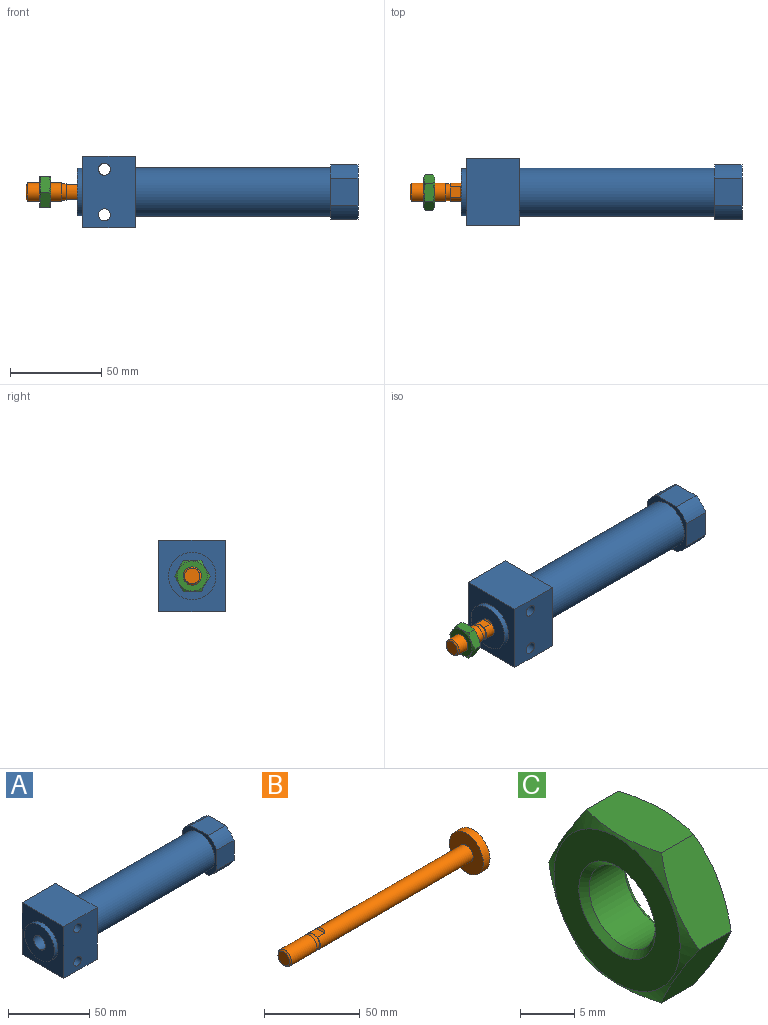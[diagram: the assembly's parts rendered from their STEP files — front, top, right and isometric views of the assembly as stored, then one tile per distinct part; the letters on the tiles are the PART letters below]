
ASSEMBLY  parts=3 mates=2
PART A: 35 faces, bbox 154x36.3x39 mm
  f0: plane 26x26mm, normal (-1,0,0), area 452.4mm2, adj f1,f25
  f1: cylinder r=13mm len=26mm, axis (1,0,0), area 245mm2, adj f0,f7
  f2: plane 39x29mm, normal (0,1,0), area 866.6mm2, adj f3,f5,f6,f7,f21,f29,f32
  f3: plane 36.3x29mm, normal (0,0,1), area 1052.7mm2, adj f2,f4,f6,f7
  f4: plane 39x29mm, normal (0,-1,0), area 1062.6mm2, adj f3,f5,f6,f7,f31,f34
  f5: plane 36.3x29mm, normal (0,0,-1), area 1052.7mm2, adj f2,f4,f6,f7
  f6: plane 39x36.3mm, normal (1,0,0), area 860mm2, adj f2,f3,f4,f5,f8
  f7: plane 39x36.3mm, normal (-1,0,0), area 884.8mm2, adj f1,f2,f3,f4,f5
  f8: cylinder r=13.3mm len=107mm, axis (-1,0,0), area 8941.6mm2, adj f6,f17
  f9: cylinder r=16.75mm len=15mm, axis (1,0,0), area 162.9mm2, adj f10,f16,f17,f18
  f10: plane 15x14.91mm, normal (0,0,1), area 223.6mm2, adj f9,f11,f17,f18
  f11: cylinder r=16.75mm len=15mm, axis (1,0,0), area 162.9mm2, adj f10,f12,f17,f18
  f12: plane 15x14.91mm, normal (0,-1,0), area 223.6mm2, adj f11,f13,f17,f18
  f13: cylinder r=16.75mm len=15mm, axis (1,0,0), area 162.9mm2, adj f12,f14,f17,f18
  f14: plane 15x14.91mm, normal (0,0,-1), area 223.6mm2, adj f13,f15,f17,f18
  f15: cylinder r=16.75mm len=15mm, axis (1,0,0), area 162.9mm2, adj f14,f16,f17,f18
  f16: plane 15x14.91mm, normal (0,1,0), area 149.3mm2, adj f9,f15,f17,f18,f24
  f17: plane 30x30mm, normal (-1,0,0), area 255.4mm2, adj f8,f9,f10,f11,f12,f13,f14,f15
  f18: plane 30x30mm, normal (1,0,0), area 811.1mm2, adj f9,f10,f11,f12,f13,f14,f15,f16
  f19: cone r=0mm half-angle=60deg, axis (0,1,0), area 66.5mm2, adj f20
  f20: cylinder r=4.28mm len=10.12mm, axis (0,1,0), area 272.3mm2, adj f19,f21
  f21: cone r=4.28mm half-angle=45deg, axis (0,1,0), area 23.6mm2, adj f2,f20
  f22: cone r=0mm half-angle=60deg, axis (0,1,0), area 66.5mm2, adj f23
  f23: cylinder r=4.28mm len=10.12mm, axis (0,1,0), area 272.3mm2, adj f22,f24
  f24: cone r=4.28mm half-angle=45deg, axis (0,1,0), area 23.6mm2, adj f16,f23
  f25: cylinder r=5mm len=32mm, axis (1,0,0), area 1005.3mm2, adj f0,f26
  f26: plane 25x25mm, normal (1,0,0), area 412.3mm2, adj f25,f27
  f27: cylinder r=12.5mm len=80mm, axis (1,0,0), area 6283.2mm2, adj f26,f28
  f28: plane 25x25mm, normal (-1,0,0), area 490.9mm2, adj f27
  f29: cylinder r=5.5mm len=11mm, axis (0,-1,0), area 259.2mm2, adj f2,f30
  f30: plane 11x11mm, normal (0,1,0), area 60.8mm2, adj f29,f31
  f31: cylinder r=3.3mm len=28.8mm, axis (0,-1,0), area 597.2mm2, adj f4,f30
  f32: cylinder r=5.5mm len=11mm, axis (0,-1,0), area 259.2mm2, adj f2,f33
  f33: plane 11x11mm, normal (0,1,0), area 60.8mm2, adj f32,f34
  f34: cylinder r=3.3mm len=28.8mm, axis (0,-1,0), area 597.2mm2, adj f4,f33
PART B: 17 faces, bbox 140x25x25 mm
  f0: plane 8x2.83mm, normal (-1,0,0), area 4.3mm2, adj f1,f7,f12,f15
  f1: cylinder r=5mm len=113mm, axis (1,0,0), area 3470.7mm2, adj f0,f2,f8,f12,f13,f14,f15
  f2: plane 8x2.83mm, normal (-1,0,0), area 4.3mm2, adj f1,f7,f12,f15
  f3: plane 8.47x8.47mm, normal (-1,0,0), area 56.3mm2, adj f4
  f4: cone r=4.23mm half-angle=45deg, axis (1,0,0), area 31.5mm2, adj f3,f5
  f5: cylinder r=5mm len=18.73mm, axis (1,0,0), area 588.5mm2, adj f4,f6
  f6: plane 10x10mm, normal (1,0,0), area 13.5mm2, adj f5,f7
  f7: cylinder r=4.55mm len=9.1mm, axis (1,0,0), area 71.5mm2, adj f0,f2,f6,f11,f16
  f8: plane 25x25mm, normal (-1,0,0), area 412.3mm2, adj f1,f9
  f9: cylinder r=12.5mm len=25mm, axis (1,0,0), area 392.7mm2, adj f8,f10
  f10: plane 25x25mm, normal (1,0,0), area 490.9mm2, adj f9
  f11: plane 4.34x0.55mm, normal (1,0,0), area 1.6mm2, adj f7,f12
  f12: plane 6x5.5mm, normal (0,0,-1), area 33mm2, adj f0,f1,f2,f11,f13
  f13: plane 6x1mm, normal (-0.71,0,-0.71), area 5.8mm2, adj f1,f12
  f14: plane 6x1mm, normal (-0.71,0,0.71), area 5.8mm2, adj f1,f15
  f15: plane 6x5.5mm, normal (0,0,1), area 33mm2, adj f0,f1,f2,f14,f16
  f16: plane 4.34x0.55mm, normal (1,0,0), area 1.6mm2, adj f7,f15
PART C: 13 faces, bbox 6x19.6x19.6 mm
  f0: plane 16.5x16.5mm, normal (1,0,0), area 135.3mm2, adj f4,f6
  f1: plane 16.5x16.5mm, normal (-1,0,0), area 135.3mm2, adj f2,f5
  f2: cone r=5mm half-angle=45deg, axis (-1,0,0), area 28mm2, adj f1,f3
  f3: cylinder r=4.32mm len=8.65mm, axis (1,0,0), area 126.2mm2, adj f2,f4
  f4: cone r=4.32mm half-angle=45deg, axis (1,0,0), area 28mm2, adj f0,f3
  f5: cone r=8.25mm half-angle=60deg, axis (1,0,0), area 42.1mm2, adj f1,f7,f8,f9,f10,f11,f12
  f6: cone r=13.45mm half-angle=60deg, axis (-1,0,0), area 42.1mm2, adj f0,f7,f8,f9,f10,f11,f12
  f7: plane 8.5x5.72mm, normal (0,0.87,0.5), area 50.9mm2, adj f5,f6,f8,f12
  f8: plane 8.5x5.72mm, normal (0,0.87,-0.5), area 50.9mm2, adj f5,f6,f7,f9
  f9: plane 9.82x5.72mm, normal (0,0,-1), area 50.9mm2, adj f5,f6,f8,f10
  f10: plane 8.5x5.72mm, normal (0,-0.87,-0.5), area 50.9mm2, adj f5,f6,f9,f11
  f11: plane 8.5x5.72mm, normal (0,-0.87,0.5), area 50.9mm2, adj f5,f6,f10,f12
  f12: plane 9.82x5.72mm, normal (0,0,1), area 50.9mm2, adj f5,f6,f7,f11
PLACE A t=(26.95,8.14,-4.22)mm
PLACE B t=(-4.05,8.14,-4.22)mm
PLACE C rot(axis=(0,0,1),180deg) t=(6.45,8.14,-4.22)mm
MATE slider B.f1 <-> A.f1  axis (1,0,0) through (135.95,8.14,-4.22)mm
MATE fastened C.f2 <-> B.f1  axis (1,0,0) through (9.45,8.14,-4.22)mm
